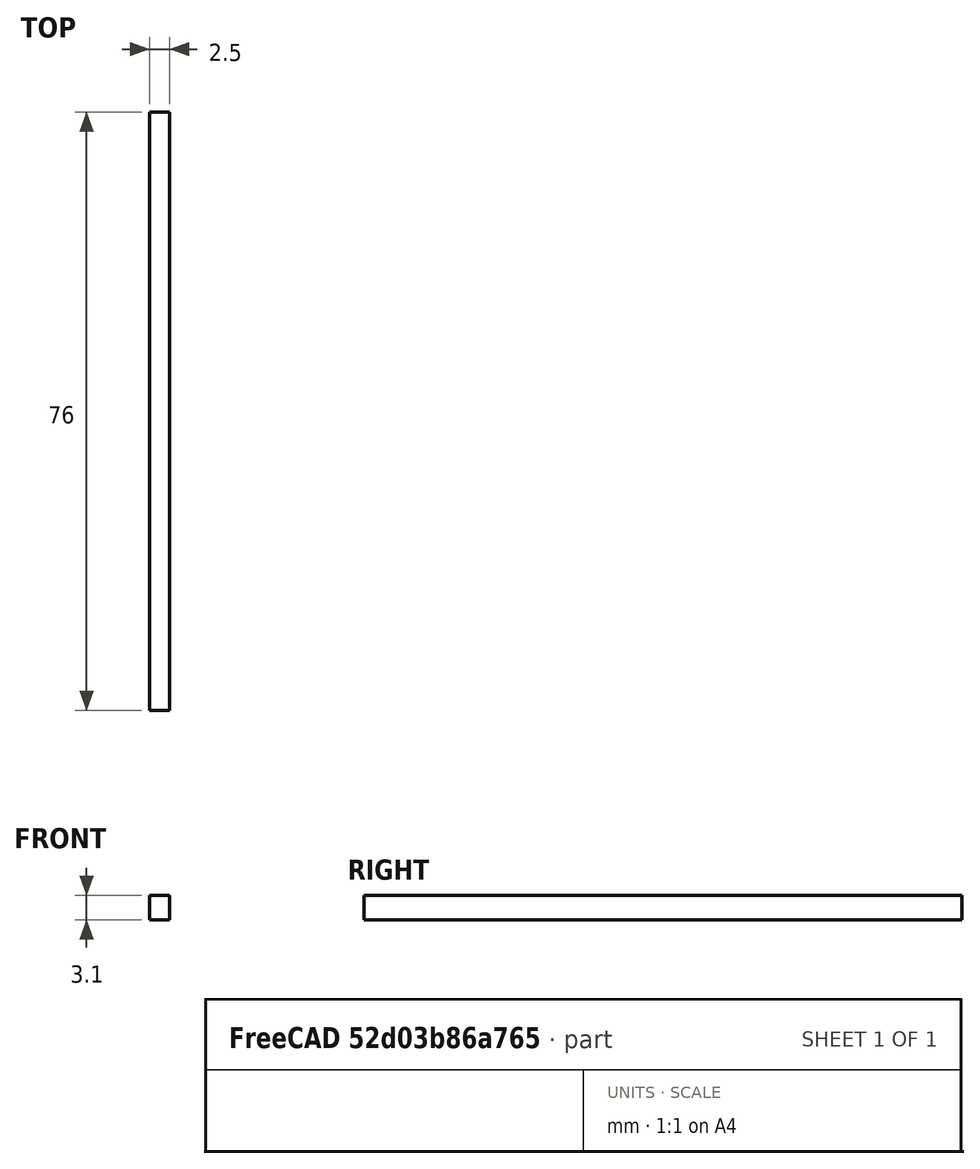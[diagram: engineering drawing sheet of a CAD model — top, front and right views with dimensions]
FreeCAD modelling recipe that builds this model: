
FCSTD DOCUMENT  (FreeCAD 1.0R39285 (Git))
Label: peltier_side_plate
License: All rights reserved
LicenseURL: https://en.wikipedia.org/wiki/All_rights_reserved
objects: Spreadsheet::Sheet×1, Sketcher::SketchObject×1, PartDesign::Pad×1, PartDesign::Body×1
note: 6 computed .brp shape members not serialized (recipe doc carries the construction recipe); baked Part::Feature solids carry a one-line shape summary decoded from their .brp

FEATURE [Spreadsheet::Sheet] Spreadsheet
  cells = A2='heat_sink_length; B2(heat_sink_length)==76 mm; A3='heat_sink_width; B3(heat_sink_width)==21 mm; A5='peltier_length; B5(peltier_length)==76 mm; A6='peltier_width; B6(peltier_width)==16 mm; A7='peltier_thickness; B7(peltier_thickness)==3.3 mm; A9='side_plate_thickness_margin; B9(side_plate_thickness_margin)==0.2 mm; A11='side_plate_length; B11(side_plate_length)==heat_sink_length; A12='side_plate_width; B12(side_plate_width)==0.5 * (heat_sink_width - peltier_width); A13='side_plate_thickness; B13(side_plate_thickness)==peltier_thickness - side_plate_thickness_margin
FEATURE [Sketcher::SketchObject] Sketch  label="SidePlateSketch"
  ArcFitTolerance = 1e-06
  AttachmentSupport = -> [XY_Plane]
  FullyConstrained = true
  MakeInternals = false
  MapMode = 5
  expr: Constraints[10] = Spreadsheet.side_plate_length
  expr: Constraints[11] = Spreadsheet.side_plate_width
  sketch-geometry (5):
    g0: LineSegment StartX=-1.25 StartY=38 StartZ=0 EndX=-1.25 EndY=-38 EndZ=0
    g1: LineSegment StartX=-1.25 StartY=-38 StartZ=0 EndX=1.25 EndY=-38 EndZ=0
    g2: LineSegment StartX=1.25 StartY=-38 StartZ=0 EndX=1.25 EndY=38 EndZ=0
    g3: LineSegment StartX=1.25 StartY=38 StartZ=0 EndX=-1.25 EndY=38 EndZ=0
    g4: GeomPoint [constr] X=0 Y=0 Z=0
  constraints (12):
    c: Coincident(g0,g1)
    c: Coincident(g1,g2)
    c: Coincident(g2,g3)
    c: Coincident(g3,g0)
    c: Vertical(g0)
    c: Vertical(g2)
    c: Horizontal(g1)
    c: Horizontal(g3)
    c: Symmetric(g2,g0,g4)
    c: Coincident(g4,g-1)
    c: DistanceY(g2,g2) = 76
    c: DistanceX(g3,g3) = 2.5
FEATURE [PartDesign::Pad] Pad  label="SidePlatePad"
  Direction = (0,0,1)
  Length = 3.1
  Length2 = 10
  Profile = -> Sketch
  ReferenceAxis = -> Sketch [N_Axis]
  Refine = true
  Suppressed = false
  Type = 0
  expr: Length = Spreadsheet.side_plate_thickness
FEATURE [PartDesign::Body] Body
  AllowCompound = false
  Group = -> [Sketch,Pad]
  Origin = -> Origin
  Tip = -> Pad
